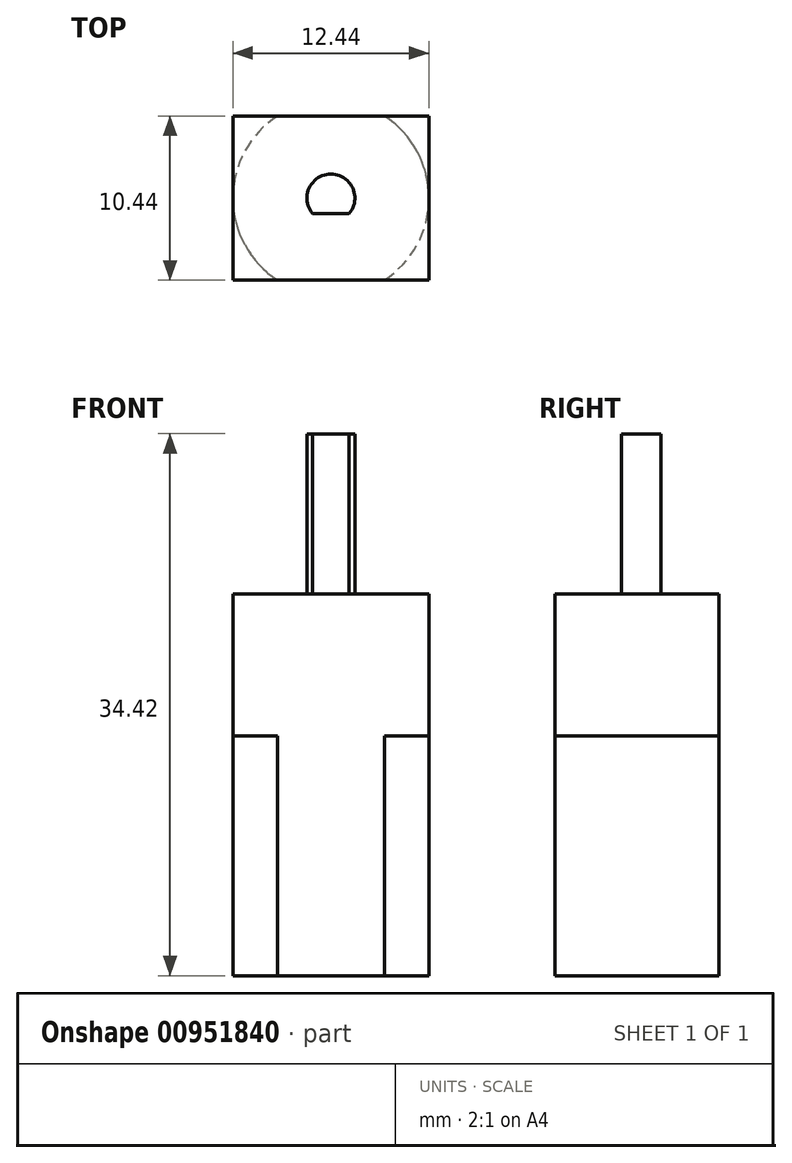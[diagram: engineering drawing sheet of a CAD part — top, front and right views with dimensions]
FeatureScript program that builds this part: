
annotation { "Feature Type Name" : "Feature", "Feature Type Description" : "" }
export const myFeature = defineFeature(function(context is Context, id is Id, definition is map)
    precondition{}
    {
        {
            var Q0;
            Q0=qCreatedBy(makeId("Top.planeOp"),FACE);
            var sketch = newSketch(context, id + "F0", { "sketchPlane" : qUnion([Q0])});
            skArc(sketch, "E0", {"start": v(-3.39, 5.22) * mm, "mid": v(-6.22, 0) * mm, "end": v(-3.39, -5.22) * mm});
            skLineSegment(sketch, "E1", {"start": v(-3.39, 5.22) * mm, "end": v(3.39, 5.22) * mm});
            skLineSegment(sketch, "E2", {"start": v(-3.39, -5.22) * mm, "end": v(3.39, -5.22) * mm});
            skArc(sketch, "E3.trimOffspring", {"start": v(3.39, -5.22) * mm, "mid": v(6.22, 0) * mm, "end": v(3.39, 5.22) * mm});
            skSolve(sketch);
        }
        {
            var Q0;
            Q0=makeQuery(id+"F0.imprint","IMPRINT",FACE,{"disambiguationData":[TD([[makeQuery(id+"F0.imprint","IMPRINT",EDGE,{"derivedFrom":sQuery(id+"F0.wireOp",EDGE,"E0")}),1.0]])]});
            extrude(context, id + "F1", {"entities" : qUnion([Q0]), "depth" : 15.24 * mm, "offsetDistance" : 25.4 * mm});
        }
        {
            var Q0;
            Q0=makeQuery(id+"F1.opExtrude","CAP_FACE",FACE,{"disambiguationData":[OSD([sQuery(id+"F0.wireOp",EDGE,"E0"),sQuery(id+"F0.wireOp",EDGE,"E1"),sQuery(id+"F0.wireOp",EDGE,"E2"),sQuery(id+"F0.wireOp",EDGE,"E3.trimOffspring")])],"isStart":false});
            var sketch = newSketch(context, id + "F2", { "sketchPlane" : qUnion([Q0])});
            skLineSegment(sketch, "E4.bottom", {"start": v(-6.22, 5.22) * mm, "end": v(6.22, 5.22) * mm});
            skLineSegment(sketch, "E4.top", {"start": v(-6.22, -5.22) * mm, "end": v(6.22, -5.22) * mm});
            skLineSegment(sketch, "E4.left", {"start": v(-6.22, 5.22) * mm, "end": v(-6.22, -5.22) * mm});
            skLineSegment(sketch, "E4.right", {"start": v(6.22, 5.22) * mm, "end": v(6.22, -5.22) * mm});
            skSolve(sketch);
        }
        {
            var Q0;
            Q0 = qSketchRegion(id + "F2", true);
            extrude(context, id + "F3", {"entities" : qUnion([Q0]), "operationType" : NewBodyOperationType.ADD, "depth" : 9.02 * mm, "offsetDistance" : 25.4 * mm});
        }
        {
            var Q0;
            Q0=makeQuery(id+"F3.opExtrude","CAP_FACE",FACE,{"disambiguationData":[OSD([sQuery(id+"F2.wireOp",EDGE,"E4.bottom"),sQuery(id+"F2.wireOp",EDGE,"E4.top"),sQuery(id+"F2.wireOp",EDGE,"E4.left"),sQuery(id+"F2.wireOp",EDGE,"E4.right")])],"isStart":false});
            var sketch = newSketch(context, id + "F4", { "sketchPlane" : qUnion([Q0])});
            skArc(sketch, "E5", {"start": v(1.16, -1) * mm, "mid": v(0, 1.52) * mm, "end": v(-1.16, -1) * mm});
            skLineSegment(sketch, "E6", {"start": v(-1.16, -1) * mm, "end": v(1.16, -1) * mm});
            skSolve(sketch);
        }
        {
            var Q0;
            Q0 = qSketchRegion(id + "F4", true);
            extrude(context, id + "F5", {"entities" : qUnion([Q0]), "operationType" : NewBodyOperationType.ADD, "depth" : 10.16 * mm, "offsetDistance" : 25.4 * mm});
        }
    });
